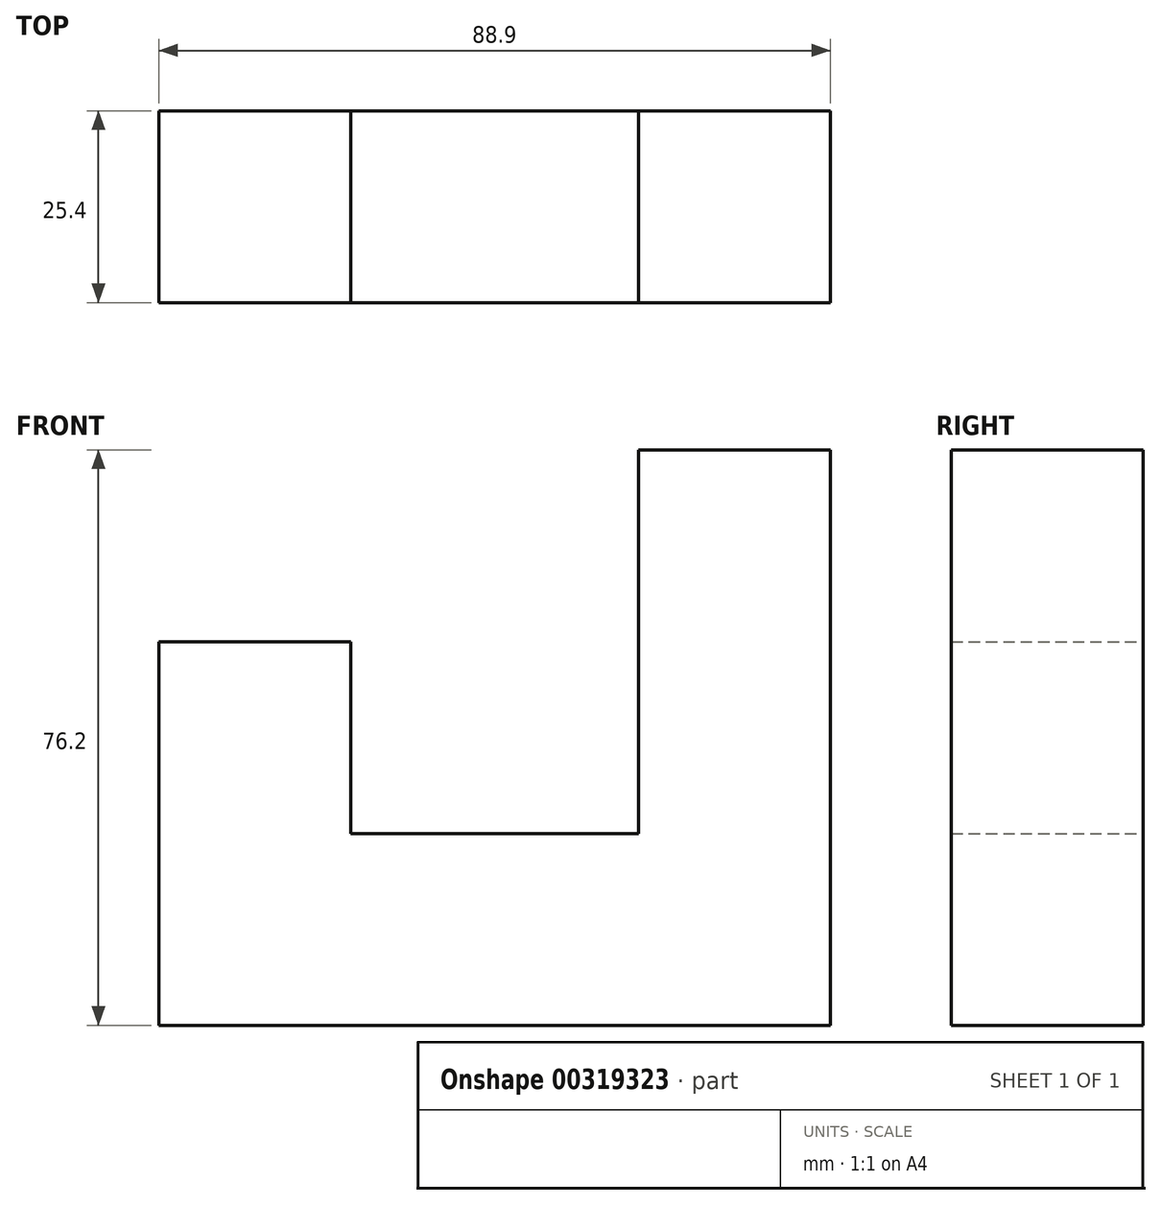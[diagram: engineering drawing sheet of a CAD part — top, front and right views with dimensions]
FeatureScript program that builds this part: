
annotation { "Feature Type Name" : "Feature", "Feature Type Description" : "" }
export const myFeature = defineFeature(function(context is Context, id is Id, definition is map)
    precondition{}
    {
        {
            var Q0;
            Q0=qCreatedBy(makeId("Front.planeOp"),FACE);
            var sketch = newSketch(context, id + "F0", { "sketchPlane" : qUnion([Q0])});
            skLineSegment(sketch, "E0", {"start": v(-42.28, -36.14) * mm, "end": v(46.62, -36.14) * mm});
            skLineSegment(sketch, "E1", {"start": v(46.62, -36.14) * mm, "end": v(46.62, 40.06) * mm});
            skLineSegment(sketch, "E2", {"start": v(46.62, 40.06) * mm, "end": v(21.22, 40.06) * mm});
            skLineSegment(sketch, "E3", {"start": v(21.22, 40.06) * mm, "end": v(21.22, -10.74) * mm});
            skLineSegment(sketch, "E4", {"start": v(21.22, -10.74) * mm, "end": v(-16.88, -10.74) * mm});
            skLineSegment(sketch, "E5", {"start": v(-16.88, -10.74) * mm, "end": v(-16.88, 14.66) * mm});
            skLineSegment(sketch, "E6", {"start": v(-16.88, 14.66) * mm, "end": v(-42.28, 14.66) * mm});
            skLineSegment(sketch, "E7", {"start": v(-42.28, 14.66) * mm, "end": v(-42.28, -36.14) * mm});
            skSolve(sketch);
        }
        {
            var Q0;
            Q0 = qSketchRegion(id + "F0", true);
            var Q1;
            Q1=makeQuery(id+"F0.imprint","IMPRINT",FACE,{"disambiguationData":[TD([[makeQuery(id+"F0.imprint","IMPRINT",EDGE,{"derivedFrom":sQuery(id+"F0.wireOp",EDGE,"E0")}),1.0]])]});
            extrude(context, id + "F1", {"entities" : qUnion([Q0, Q1]), "depth" : 25.4 * mm});
        }
    });
